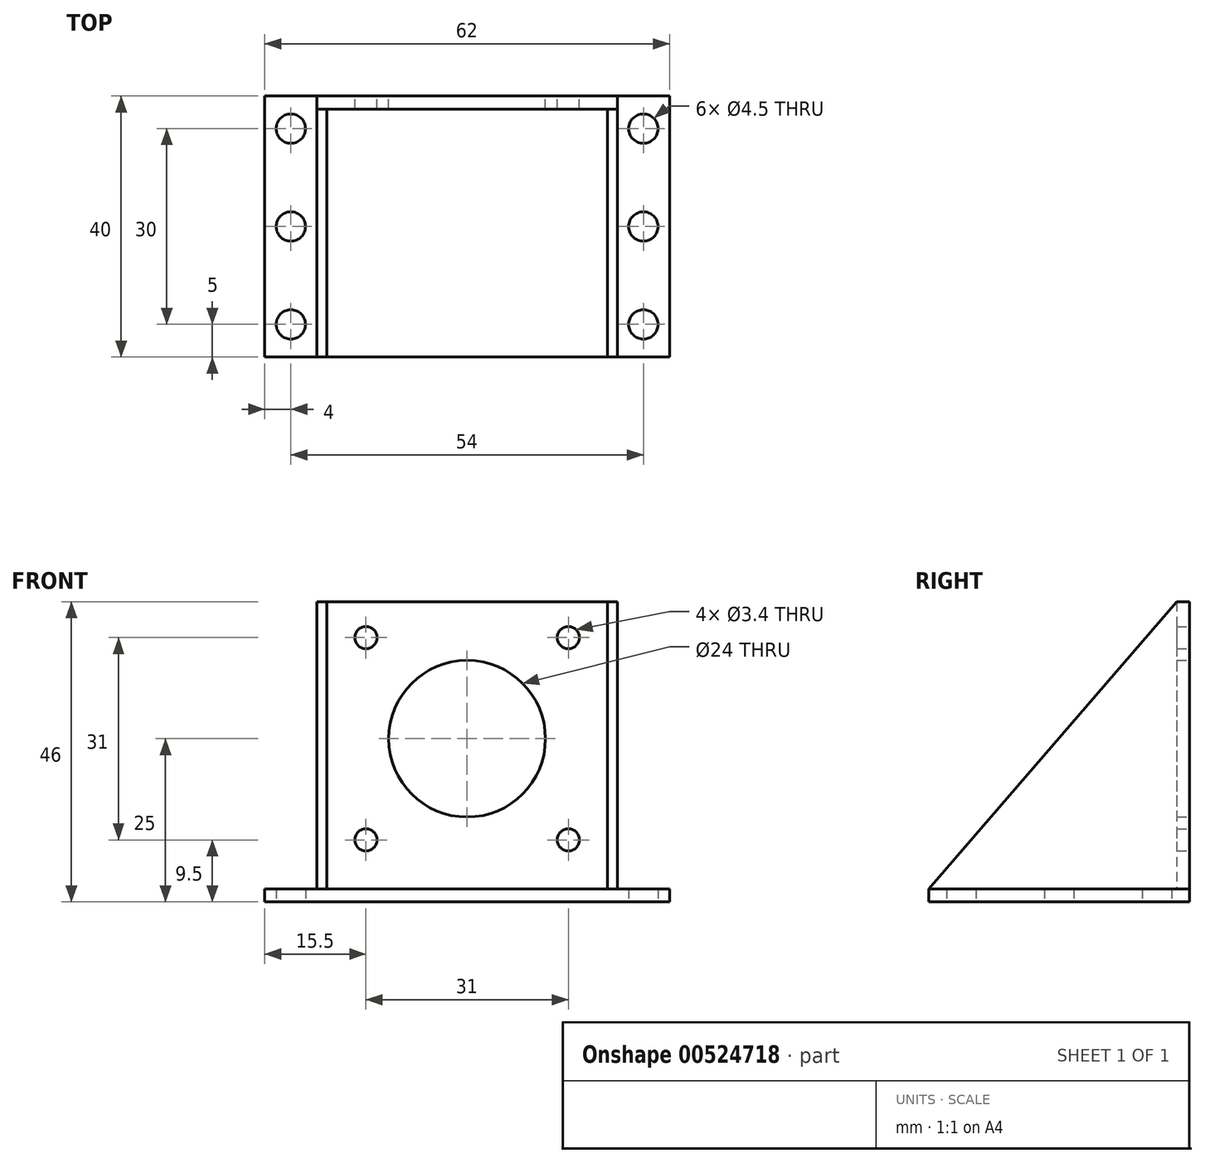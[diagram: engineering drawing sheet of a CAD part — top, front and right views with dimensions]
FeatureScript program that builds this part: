
annotation { "Feature Type Name" : "Feature", "Feature Type Description" : "" }
export const myFeature = defineFeature(function(context is Context, id is Id, definition is map)
    precondition{}
    {
        {
            var Q0;
            Q0=qCreatedBy(makeId("Top.planeOp"),FACE);
            var sketch = newSketch(context, id + "F0", { "sketchPlane" : qUnion([Q0])});
            skLineSegment(sketch, "E0.bottom", {"start": v(-31, 20) * mm, "end": v(31, 20) * mm});
            skLineSegment(sketch, "E0.top", {"start": v(-31, -20) * mm, "end": v(31, -20) * mm});
            skLineSegment(sketch, "E0.left", {"start": v(-31, 20) * mm, "end": v(-31, -20) * mm});
            skLineSegment(sketch, "E0.right", {"start": v(31, 20) * mm, "end": v(31, -20) * mm});
            skCircle(sketch, "E1", {"center": v(-27, 15) * mm, "radius": 2.25 * mm});
            skCircle(sketch, "E2", {"center": v(-27, 0) * mm, "radius": 2.25 * mm});
            skCircle(sketch, "E3", {"center": v(27, 15) * mm, "radius": 2.25 * mm});
            skCircle(sketch, "E4", {"center": v(27, 0) * mm, "radius": 2.25 * mm});
            skLineSegment(sketch, "E5", {"start": v(-27, 27.44) * mm, "end": v(-27, -31.47) * mm, "construction": true});
            skLineSegment(sketch, "E6", {"start": v(27, 27.1) * mm, "end": v(27, -32.16) * mm, "construction": true});
            skLineSegment(sketch, "E7", {"start": v(-43.4, 15) * mm, "end": v(40.48, 15) * mm, "construction": true});
            skLineSegment(sketch, "E8", {"start": v(-43.23, 0) * mm, "end": v(39.79, 0) * mm, "construction": true});
            skLineSegment(sketch, "E9", {"start": v(-42.93, -15) * mm, "end": v(39.55, -15) * mm, "construction": true});
            skCircle(sketch, "E10", {"center": v(-27, -15) * mm, "radius": 2.25 * mm});
            skCircle(sketch, "E11", {"center": v(27, -15) * mm, "radius": 2.25 * mm});
            skSolve(sketch);
        }
        {
            var Q0;
            Q0 = qSketchRegion(id + "F0", true);
            extrude(context, id + "F1", {"entities" : qUnion([Q0]), "depth" : 2 * mm, "offsetDistance" : 25 * mm});
        }
        {
            var Q0;
            Q0=makeQuery(id+"F1.opExtrude","SWEPT_FACE",FACE,{"disambiguationData":[OSD([sQuery(id+"F0.wireOp",EDGE,"E0.bottom")])]});
            cPlane(context, id + "F2", {"entities" : qUnion([Q0]), "cplaneType" : CPlaneType.OFFSET, "offset" : 0 * mm, "width" : 150 * mm, "height" : 150 * mm});
        }
        {
            var Q0;
            Q0=qCreatedBy(id+"F2.planeOp",FACE);
            var sketch = newSketch(context, id + "F3", { "sketchPlane" : qUnion([Q0])});
            skLineSegment(sketch, "E12.bottom", {"start": v(-23, 46) * mm, "end": v(23, 46) * mm});
            skLineSegment(sketch, "E12.top", {"start": v(-23, 2) * mm, "end": v(23, 2) * mm});
            skLineSegment(sketch, "E12.left", {"start": v(-23, 46) * mm, "end": v(-23, 2) * mm});
            skLineSegment(sketch, "E12.right", {"start": v(23, 46) * mm, "end": v(23, 2) * mm});
            skLineSegment(sketch, "E13.0", {"start": v(31, 2) * mm, "end": v(-31, 2) * mm, "construction": true});
            skLineSegment(sketch, "E14", {"start": v(-27.24, 9.5) * mm, "end": v(29.41, 9.5) * mm, "construction": true});
            skLineSegment(sketch, "E15", {"start": v(-29.26, 25) * mm, "end": v(30.82, 25) * mm, "construction": true});
            skLineSegment(sketch, "E16", {"start": v(-29.66, 40.5) * mm, "end": v(30.92, 40.5) * mm, "construction": true});
            skLineSegment(sketch, "E17", {"start": v(-15.5, 49.36) * mm, "end": v(-15.5, -4.37) * mm, "construction": true});
            skLineSegment(sketch, "E18", {"start": v(15.5, 49.26) * mm, "end": v(15.5, -4.38) * mm, "construction": true});
            skCircle(sketch, "E19", {"center": v(0, 25) * mm, "radius": 12 * mm});
            skCircle(sketch, "E20", {"center": v(-15.5, 40.5) * mm, "radius": 1.7 * mm});
            skCircle(sketch, "E21", {"center": v(15.5, 40.5) * mm, "radius": 1.7 * mm});
            skCircle(sketch, "E22", {"center": v(-15.5, 9.5) * mm, "radius": 1.7 * mm});
            skCircle(sketch, "E23", {"center": v(15.5, 9.5) * mm, "radius": 1.7 * mm});
            skSolve(sketch);
        }
        {
            var Q0;
            Q0 = qSketchRegion(id + "F3", true);
            extrude(context, id + "F4", {"entities" : qUnion([Q0]), "operationType" : NewBodyOperationType.ADD, "oppositeDirection" : true, "depth" : 2 * mm, "offsetDistance" : 25 * mm});
        }
        {
            var Q0;
            Q0=makeQuery(id+"F4.opExtrude","SWEPT_FACE",FACE,{"disambiguationData":[OSD([sQuery(id+"F3.wireOp",EDGE,"E12.left")])]});
            var sketch = newSketch(context, id + "F5", { "sketchPlane" : qUnion([Q0])});
            skLineSegment(sketch, "E24.0", {"start": v(18, 46) * mm, "end": v(18, 2) * mm});
            skLineSegment(sketch, "E25.0", {"start": v(18, 2) * mm, "end": v(-20, 2) * mm});
            skPoint(sketch, "E26.orphan", {"position": v(20, 2) * mm});
            skLineSegment(sketch, "E27", {"start": v(18, 46) * mm, "end": v(-20, 2) * mm});
            skSolve(sketch);
        }
        {
            var Q0;
            Q0 = qSketchRegion(id + "F5", true);
            extrude(context, id + "F6", {"entities" : qUnion([Q0]), "oppositeDirection" : true, "depth" : 1.5 * mm, "offsetDistance" : 25 * mm});
        }
        {
            var Q0;
            Q0=makeQuery(id+"F6.opExtrude","SWEPT_BODY",BODY,{"disambiguationData":[OSD([sQuery(id+"F5.wireOp",EDGE,"E24.0"),sQuery(id+"F5.wireOp",EDGE,"E25.0"),sQuery(id+"F5.wireOp",EDGE,"E27")])]});
            var Q1;
            Q1=qCreatedBy(makeId("Right.planeOp"),FACE);
            mirror(context, id + "F7", {"operationType" : NewBodyOperationType.ADD, "entities" : qUnion([Q0]), "mirrorPlane" : qUnion([Q1])});
        }
    });
